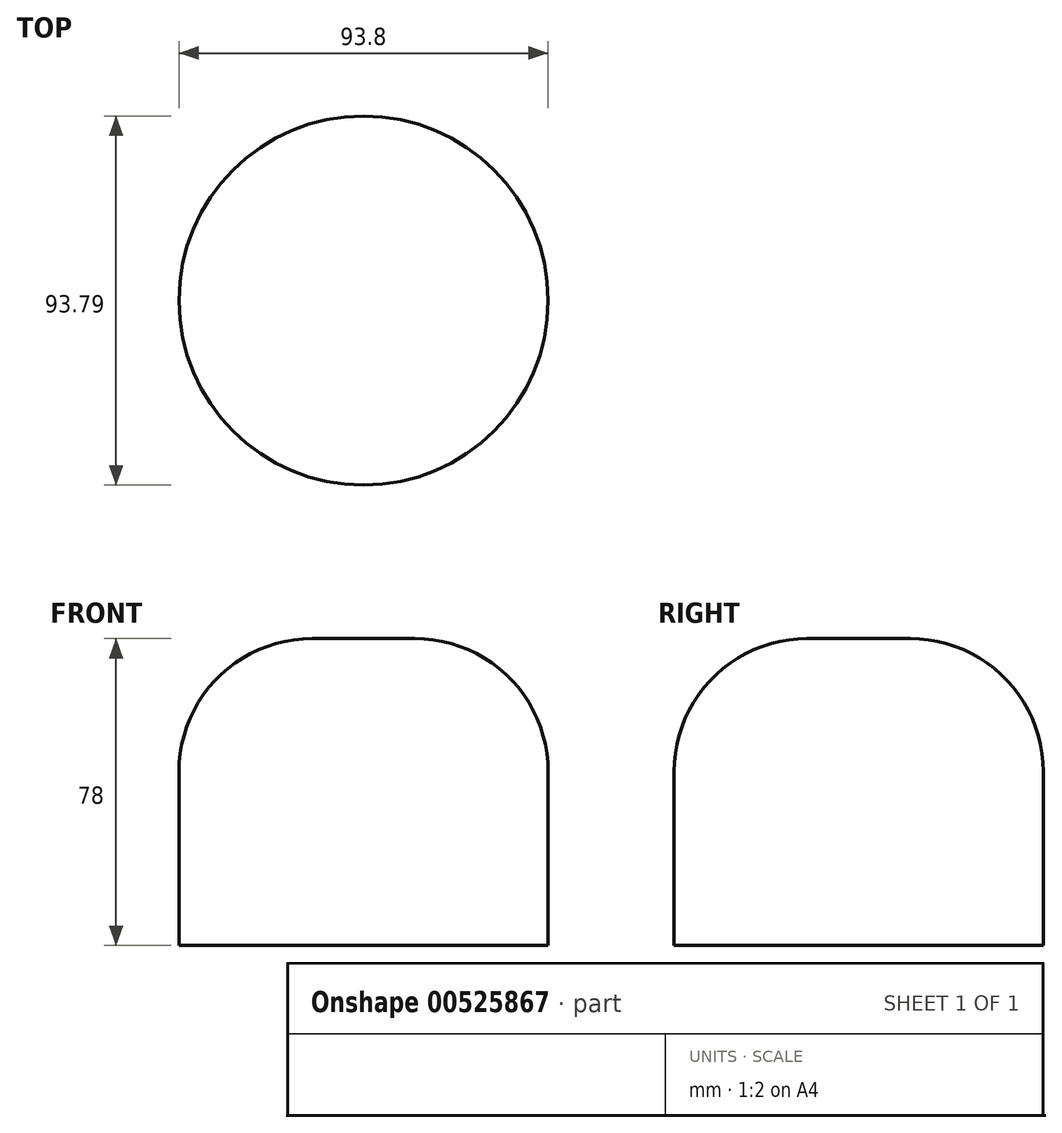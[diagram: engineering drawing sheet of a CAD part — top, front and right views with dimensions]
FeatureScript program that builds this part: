
annotation { "Feature Type Name" : "Feature", "Feature Type Description" : "" }
export const myFeature = defineFeature(function(context is Context, id is Id, definition is map)
    precondition{}
    {
        {
            var Q0;
            Q0=qCreatedBy(makeId("Top.planeOp"),FACE);
            var sketch = newSketch(context, id + "F0", { "sketchPlane" : qUnion([Q0])});
            skCircle(sketch, "E0", {"center": v(0, 9.06) * mm, "radius": 46.9 * mm});
            skSolve(sketch);
        }
        {
            var Q0;
            Q0=makeQuery(id+"F0.imprint","IMPRINT",FACE,{"disambiguationData":[TD([[makeQuery(id+"F0.imprint","IMPRINT",EDGE,{"derivedFrom":sQuery(id+"F0.wireOp",EDGE,"E0")}),1.0]])]});
            extrude(context, id + "F1", {"entities" : qUnion([Q0]), "depth" : 25 * mm, "offsetDistance" : 25 * mm});
        }
        {
            var Q0;
            Q0=makeQuery(id+"F1.opExtrude","CAP_FACE",FACE,{"disambiguationData":[OSD([sQuery(id+"F0.wireOp",EDGE,"E0")])],"isStart":false});
            extrude(context, id + "F2", {"entities" : qUnion([Q0]), "operationType" : NewBodyOperationType.ADD, "depth" : 53 * mm, "offsetDistance" : 25 * mm});
        }
        {
            var Q0;
            Q0=makeQuery(id+"F2.opExtrude","CAP_EDGE",EDGE,{"disambiguationData":[OSD([sQuery(id+"F0.wireOp",EDGE,"E0")])],"isStart":false});
            fillet(context, id + "F3", {"entities" : qUnion([Q0]), "radius" : 33.8 * mm, "tangentPropagation" : true, "allowEdgeOverflow" : false});
        }
    });
